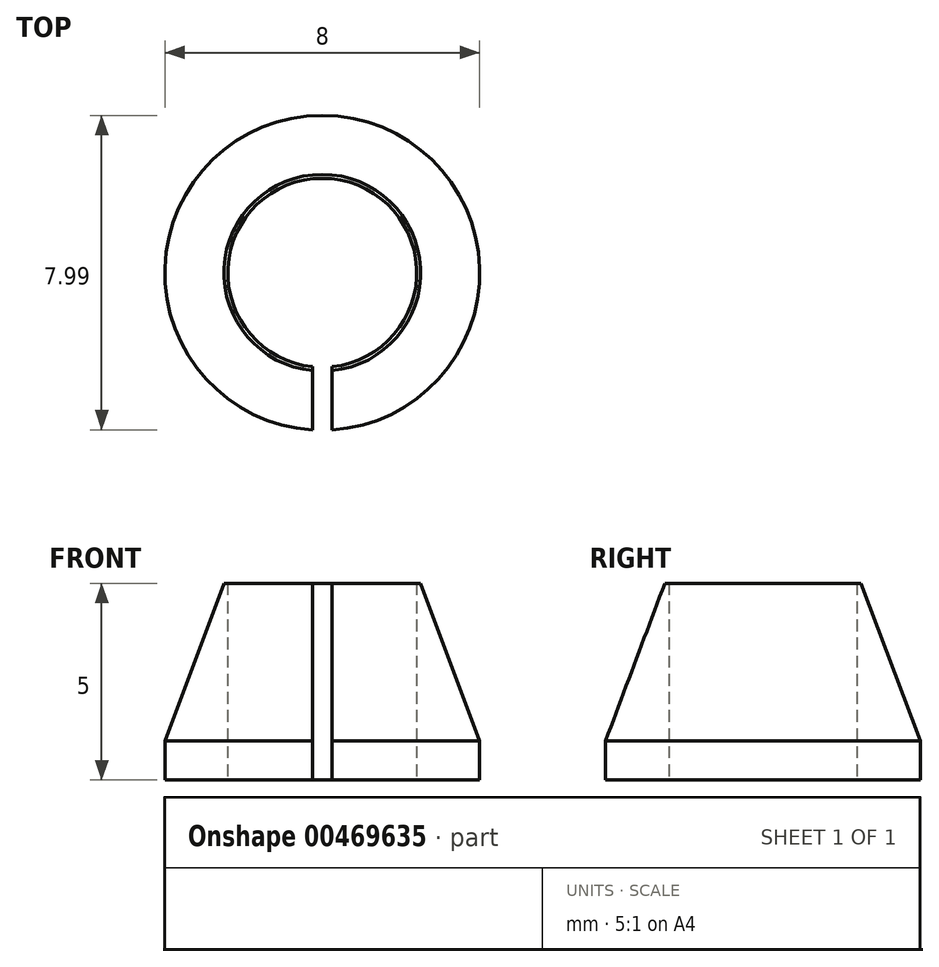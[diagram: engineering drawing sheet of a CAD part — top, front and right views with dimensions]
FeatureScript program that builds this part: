
annotation { "Feature Type Name" : "Feature", "Feature Type Description" : "" }
export const myFeature = defineFeature(function(context is Context, id is Id, definition is map)
    precondition{}
    {
        {
            var Q0;
            Q0=qCreatedBy(makeId("Front.planeOp"),FACE);
            var sketch = newSketch(context, id + "F0", { "sketchPlane" : qUnion([Q0])});
            skLineSegment(sketch, "E0", {"start": v(0, -29.65) * mm, "end": v(0, 0) * mm, "construction": true});
            skLineSegment(sketch, "E1", {"start": v(-2.4, 5) * mm, "end": v(-2.5, 5) * mm});
            skLineSegment(sketch, "E2", {"start": v(-2.5, 5) * mm, "end": v(-4, 1) * mm});
            skLineSegment(sketch, "E3", {"start": v(-4, 1) * mm, "end": v(-4, 0) * mm});
            skLineSegment(sketch, "E4", {"start": v(-4, 0) * mm, "end": v(-2.4, 0) * mm});
            skLineSegment(sketch, "E5", {"start": v(-2.4, 5) * mm, "end": v(-2.4, 0) * mm});
            skLineSegment(sketch, "E6.trimOffspring", {"start": v(0, 5) * mm, "end": v(0, 38.5) * mm, "construction": true});
            skSolve(sketch);
        }
        {
            var Q0;
            Q0 = qSketchRegion(id + "F0", true);
            var Q1;
            Q1=sQuery(id+"F0.wireOp",EDGE,"E0");
            revolve(context, id + "F1", {"entities" : qUnion([Q0]), "axis" : qUnion([Q1]), "revolveType" : RevolveType.FULL});
        }
        {
            var Q0;
            Q0=makeQuery(id+"F1.opRevolve","SWEPT_FACE",FACE,{"disambiguationData":[OSD([sQuery(id+"F0.wireOp",EDGE,"E4")])]});
            var sketch = newSketch(context, id + "F2", { "sketchPlane" : qUnion([Q0])});
            skLineSegment(sketch, "E7.bottom", {"start": v(0.25, 0.6) * mm, "end": v(-0.25, 0.6) * mm});
            skLineSegment(sketch, "E7.top", {"start": v(0.25, 5.6) * mm, "end": v(-0.25, 5.6) * mm});
            skLineSegment(sketch, "E7.left", {"start": v(0.25, 0.6) * mm, "end": v(0.25, 5.6) * mm});
            skLineSegment(sketch, "E7.right", {"start": v(-0.25, 0.6) * mm, "end": v(-0.25, 5.6) * mm});
            skPoint(sketch, "E7.middle", {"position": v(0, 3.1) * mm});
            skSolve(sketch);
        }
        {
            var Q0;
            Q0 = qSketchRegion(id + "F2", true);
            extrude(context, id + "F3", {"entities" : qUnion([Q0]), "operationType" : NewBodyOperationType.REMOVE, "oppositeDirection" : true, "depth" : 25 * mm});
        }
    });
